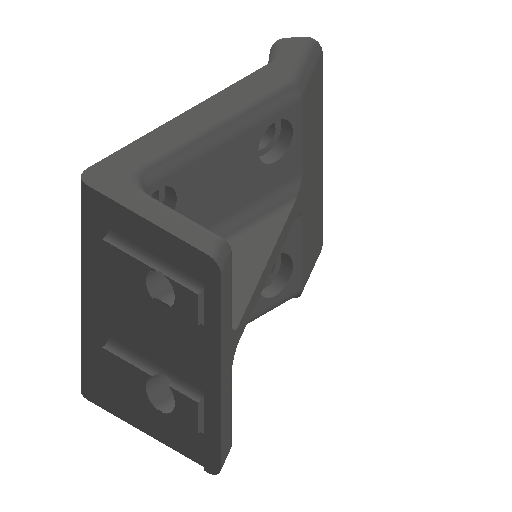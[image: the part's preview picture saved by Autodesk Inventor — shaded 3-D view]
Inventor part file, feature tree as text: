
AUTODESK INVENTOR PART (.ipt)
format: ipt  version: 2024.1 (Build 281209000, 209)  size: 911,360 bytes
history: native  units: in
note: dims shown in document units (in); Inventor stores cm internally (conversion verified against a paired STEP export)
features: extrude x6, projected_geometry x3, sketch x2, hole x2, fillet x2, plane x1
ambient origin geometry x8: Origin, YZ Plane, XZ Plane, XY Plane, X Axis, Y Axis, Z Axis, Center Point
bodies: Solid1 (feature_tree)
feature tree (16):
  sketch  "Sketch1"  dims[d0=0.165in d1=0.165in]
  extrude  "Extrusion1"  Depth=0.165in
  extrude  "Extrusion2"  Depth=0.0625in TaperAngle=0.0deg
  extrude  "Extrusion3"  Depth=0.25in
  hole  "Hole1"  [1 undecoded]
  hole  "Hole2"  [1 undecoded]
  fillet  "Fillet1"  Radius=0.008in
  plane  "Work Plane1"
  extrude  "Extrusion6"  Depth=0.008in
  extrude  "Extrusion7"  Depth=0.008in
  extrude  "Extrusion8"  Depth=1.5in TaperAngle=0.0deg
  fillet  "Fillet8"  Radius=0.5in
  sketch  "Sketch2"  dims[d2=0.3125in d3=0.0in d4=0.0625in d5=0.0in d6=0.25in d8=1.5748in d9=0.7874in d10=0.7874in d11=0.1969in d12=0.2402in d13=0.2402in d14=0.2441in d15=0.0551in d16=0.0276in d17=45.0deg d18=0.0551in d19=360.0deg d20=0.0394in d22=0.0157in d23=0.0157in d24=0.008in d25=0.008in d26=0.008in d27=0.008in d29=1.5in d30=0.0in d31=0.5in d32=0.75in d33=0.25in d34=0.75in d35=0.435in d36=0.125in d37=0.5635in d38=1.0in d39=0.0in d40=0.2in d41=0.75in d42=0.3in d43=0.1in d44=0.5635in d45=1.0in d46=0.0in d47=0.125in d49=0.3in d50=0.3in d51=0.7874in d52=0.375in d53=0.625in d54=0.8071in d58=-0.8125in d67=0.825in d68=0.0in d69=0.0in d70=0.125in d71=0.0in d72=1.625in d73=0.0in d74=0.1in d79=0.2749in d55=0.0in d56=0.0in d57=0.0in]
  projected_geometry  "Projected Loop1"
  projected_geometry  "Projected Loop3"
  projected_geometry  "Projected Loop4"
note: 2 required parameter values undecoded (feature->parameter linkage not recoverable at this tier; creation-order binding heuristic only, values carry confidence <= 0.55)
